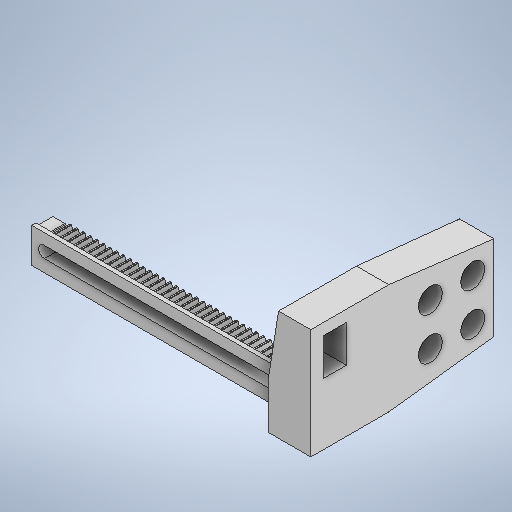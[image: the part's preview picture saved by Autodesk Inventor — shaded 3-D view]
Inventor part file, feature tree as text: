
AUTODESK INVENTOR PART (.ipt)
format: ipt  version: 2025.1 (Build 291241000, 241)  size: 1,479,680 bytes
history: native  units: mm
features: sketch x18, extrude x16, projected_geometry x8, chamfer x4, plane x1
ambient origin geometry x8: Origin, YZ Plane, XZ Plane, XY Plane, X Axis, Y Axis, Z Axis, Center Point
bodies: Solid1 (feature_tree)
feature tree (47):
  extrude  "Extrusion1"  Depth=0.785398mm
  extrude  "Extrusion2"  Depth=1.125mm
  chamfer  "Chamfer1"  Distance=350.0mm
  chamfer  "Chamfer2"  Distance=10.0mm
  sketch  "Sketch3"  dims[d7=0.25mm]
  extrude  "Extrusion3"  Depth=3.0mm
  extrude  "Extrusion4"  Depth=0.2mm
  extrude  "Extrusion5"  Depth=40.0mm
  extrude  "Extrusion6"  Depth=10.0mm
  extrude  "Extrusion7"  Depth=10.0mm
  extrude  "Extrusion8"  Depth=5.6mm
  extrude  "Extrusion9"  Depth=7.0mm TaperAngle=0.0deg
  extrude  "Extrusion10"  Depth=12.4999mm TaperAngle=45.0deg
  extrude  "Extrusion11"  Depth=2.7mm
  chamfer  "Chamfer3"  Distance=7.0mm
  extrude  "Extrusion12"  Depth=3.0mm
  extrude  "Extrusion13"  Depth=3.0mm
  sketch  "Sketch15"  dims[d45=14.0mm d46=2.0mm d47=45.0deg d48=2.7mm]
  plane  "Work Plane1"
  extrude  "Extrusion14"  Depth=3.0mm TaperAngle=0.0deg
  chamfer  "Chamfer4"  Distance=8.2mm
  extrude  "Extrusion15"  Depth=3.0mm TaperAngle=0.0deg
  extrude  "Extrusion16"  Depth=3.0mm TaperAngle=0.0deg
  sketch  "Sketch1"  dims[d1=0.785398mm d2=0.785398mm]
  sketch  "Sketch Rectangular Pattern1"  dims[d3=1.570796mm d4=1.125mm]
  sketch  "Sketch2"  dims[d5=0.5mm]
  projected_geometry  "Projected Loop1"
  sketch  "Sketch Rectangular Pattern2"  dims[d6=12.217305mm]
  projected_geometry  "Projected Loop2"
  sketch  "Sketch4"  dims[d8=0.1mm d9=350.0mm d11=1.570796mm d12=10.0mm d14=10.0mm]
  sketch  "Sketch5"  dims[d16=3.0mm d17=3.0mm]
  projected_geometry  "Projected Loop3"
  sketch  "Sketch6"  dims[d20=60.977871mm d21=0.2mm]
  projected_geometry  "Projected Loop4"
  sketch  "Sketch7"  dims[d22=5.0mm d23=0.0mm d24=40.0mm]
  projected_geometry  "Projected Loop5"
  sketch  "Sketch10"  dims[d25=20.0mm d26=10.0mm]
  sketch  "Sketch11"  dims[d27=5.0mm d28=10.0mm]
  sketch  "Sketch12"  dims[d29=5.0mm d30=5.6mm]
  sketch  "Sketch13"  dims[d31=20.0mm d33=10.0mm d34=20.0mm d36=10.0mm d39=7.0mm d40=0.0mm]
  sketch  "Sketch14"  dims[d41=7.5mm d42=12.4999mm d43=2.0mm d44=45.0deg]
  sketch  "Sketch16"  dims[d49=3.0mm]
  projected_geometry  "Projected Loop6"
  sketch  "Sketch17"  dims[d50=3.0mm d51=7.0mm d52=0.0mm]
  projected_geometry  "Projected Loop7"
  sketch  "Sketch18"  dims[d53=10.0mm d54=11.5mm d55=0.5mm d56=0.3mm d57=0.0mm d58=8.2mm d59=10.0mm d60=0.0mm d61=0.2mm d62=0.0mm d63=0.2mm d64=0.0mm d65=3.0mm d66=3.0mm d67=0.0mm d68=0.0mm d69=0.0mm d70=10.0mm d71=0.0mm d72=10.0mm d73=0.0mm d74=24.8mm d75=3.0mm d76=45.0deg d77=0.25mm d78=0.0mm d79=0.2mm d80=0.0mm d81=1.0mm d82=0.0mm d83=0.785398mm d84=0.785398mm d85=90.0deg d86=18.4mm d87=3.0mm d88=0.0mm d89=24.8mm d90=3.0mm d91=45.0deg d92=0.5mm d93=1.1mm d94=0.0mm d95=0.3mm d96=0.0mm]
  projected_geometry  "Projected Loop8"
